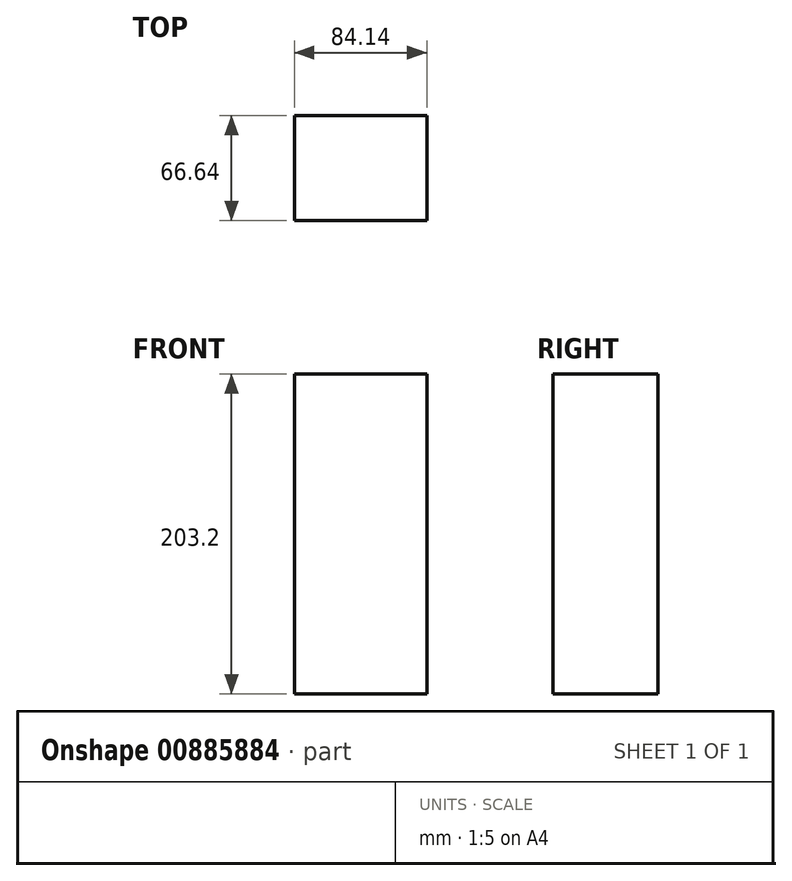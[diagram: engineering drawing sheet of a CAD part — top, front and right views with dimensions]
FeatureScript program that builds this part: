
annotation { "Feature Type Name" : "Feature", "Feature Type Description" : "" }
export const myFeature = defineFeature(function(context is Context, id is Id, definition is map)
    precondition{}
    {
        {
            var Q0;
            Q0=qCreatedBy(makeId("Top.planeOp"),FACE);
            var sketch = newSketch(context, id + "F0", { "sketchPlane" : qUnion([Q0])});
            skLineSegment(sketch, "E0.bottom", {"start": v(-42.07, 33.32) * mm, "end": v(42.07, 33.32) * mm});
            skLineSegment(sketch, "E0.top", {"start": v(-42.07, -33.32) * mm, "end": v(42.07, -33.32) * mm});
            skLineSegment(sketch, "E0.left", {"start": v(-42.07, 33.32) * mm, "end": v(-42.07, -33.32) * mm});
            skLineSegment(sketch, "E0.right", {"start": v(42.07, 33.32) * mm, "end": v(42.07, -33.32) * mm});
            skPoint(sketch, "E0.middle", {"position": v(0, 0) * mm});
            skSolve(sketch);
        }
        {
            var Q0;
            Q0 = qSketchRegion(id + "F0", true);
            extrude(context, id + "F1", {"entities" : qUnion([Q0]), "depth" : 203.2 * mm, "offsetDistance" : 25.4 * mm});
        }
    });
